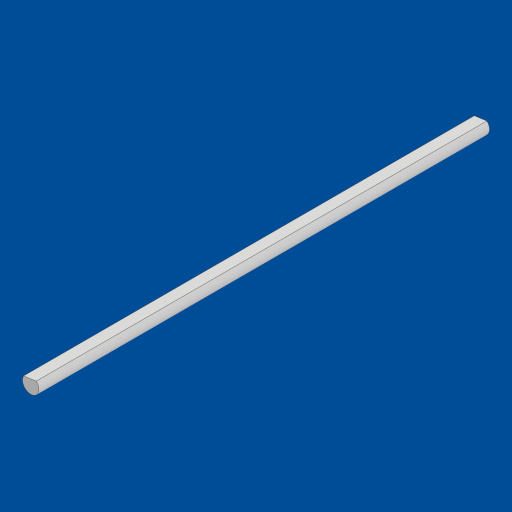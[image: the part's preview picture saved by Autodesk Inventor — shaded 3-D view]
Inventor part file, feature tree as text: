
AUTODESK INVENTOR PART (.ipt)
format: ipt  version: 2023.1 (Build 271208000, 208)  size: 87,552 bytes
history: native  units: mm
features: extrude x1, sketch x1
ambient origin geometry x8: Origin, YZ Plane, XZ Plane, XY Plane, X Axis, Y Axis, Z Axis, Center Point
bodies: Solid1 (feature_tree)
feature tree (2):
  extrude  "Extrusion1"  Depth=89.6mm
  sketch  "Sketch1"  dims[d0=3.25mm d1=1.025mm d2=89.6mm d3=0.0mm]
